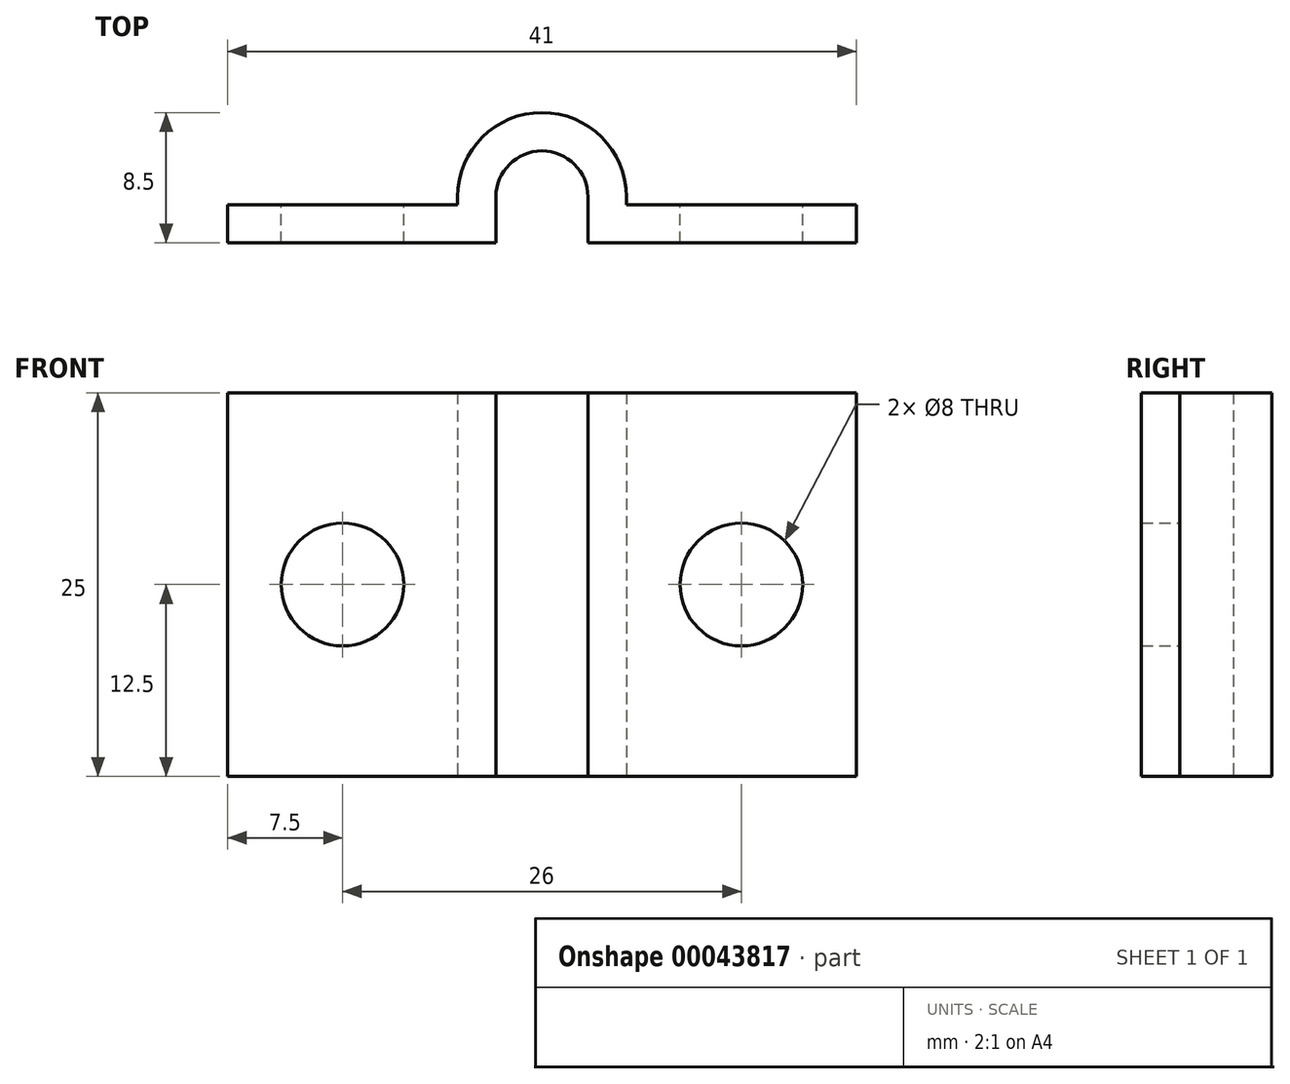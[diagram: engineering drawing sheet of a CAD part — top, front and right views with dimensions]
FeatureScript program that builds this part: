
annotation { "Feature Type Name" : "Feature", "Feature Type Description" : "" }
export const myFeature = defineFeature(function(context is Context, id is Id, definition is map)
    precondition{}
    {
        {
            var Q0;
            Q0=qCreatedBy(makeId("Top.planeOp"),FACE);
            var sketch = newSketch(context, id + "F0", { "sketchPlane" : qUnion([Q0])});
            skArc(sketch, "E0", {"start": v(3, 3) * mm, "mid": v(0, 6) * mm, "end": v(-3, 3) * mm});
            skLineSegment(sketch, "E1", {"start": v(-3, 3) * mm, "end": v(-3, 0) * mm});
            skLineSegment(sketch, "E2", {"start": v(3, 3) * mm, "end": v(3, 0) * mm});
            skLineSegment(sketch, "E3", {"start": v(-3, 0) * mm, "end": v(-5.5, 0) * mm});
            skLineSegment(sketch, "E4", {"start": v(3, 0) * mm, "end": v(5.5, 0) * mm});
            skArc(sketch, "E5", {"start": v(5.5, 3) * mm, "mid": v(0, 8.5) * mm, "end": v(-5.5, 3) * mm});
            skLineSegment(sketch, "E6", {"start": v(-5.5, 2.5) * mm, "end": v(-5.5, 3) * mm});
            skLineSegment(sketch, "E7", {"start": v(5.5, 2.5) * mm, "end": v(5.5, 3) * mm});
            skLineSegment(sketch, "E8.bottom", {"start": v(-5.5, 0) * mm, "end": v(-20.5, 0) * mm});
            skLineSegment(sketch, "E8.top", {"start": v(-5.5, 2.5) * mm, "end": v(-20.5, 2.5) * mm});
            skLineSegment(sketch, "E8.right", {"start": v(-20.5, 0) * mm, "end": v(-20.5, 2.5) * mm});
            skLineSegment(sketch, "E9.bottom", {"start": v(5.5, 0) * mm, "end": v(20.5, 0) * mm});
            skLineSegment(sketch, "E9.top", {"start": v(5.5, 2.5) * mm, "end": v(20.5, 2.5) * mm});
            skLineSegment(sketch, "E9.right", {"start": v(20.5, 0) * mm, "end": v(20.5, 2.5) * mm});
            skSolve(sketch);
        }
        {
            var Q0;
            Q0 = qSketchRegion(id + "F0", true);
            extrude(context, id + "F1", {"entities" : qUnion([Q0]), "depth" : 25 * mm});
        }
        {
            var Q0;
            Q0=makeQuery(id+"F1.opExtrude","SWEPT_FACE",FACE,{"disambiguationData":[OSD([sQuery(id+"F0.wireOp",EDGE,"E9.top")])]});
            var sketch = newSketch(context, id + "F2", { "sketchPlane" : qUnion([Q0])});
            skCircle(sketch, "E10", {"center": v(13, 12.5) * mm, "radius": 4 * mm});
            skCircle(sketch, "E11", {"center": v(-13, 12.5) * mm, "radius": 4 * mm});
            skLineSegment(sketch, "E12.0", {"start": v(5.5, 0) * mm, "end": v(20.5, 0) * mm});
            skLineSegment(sketch, "E13", {"start": v(13, 0) * mm, "end": v(13, 25) * mm, "construction": true});
            skSolve(sketch);
        }
        {
            var Q0;
            Q0 = qSketchRegion(id + "F2", true);
            extrude(context, id + "F3", {"entities" : qUnion([Q0]), "operationType" : NewBodyOperationType.REMOVE, "oppositeDirection" : true, "depth" : 25 * mm});
        }
    });
